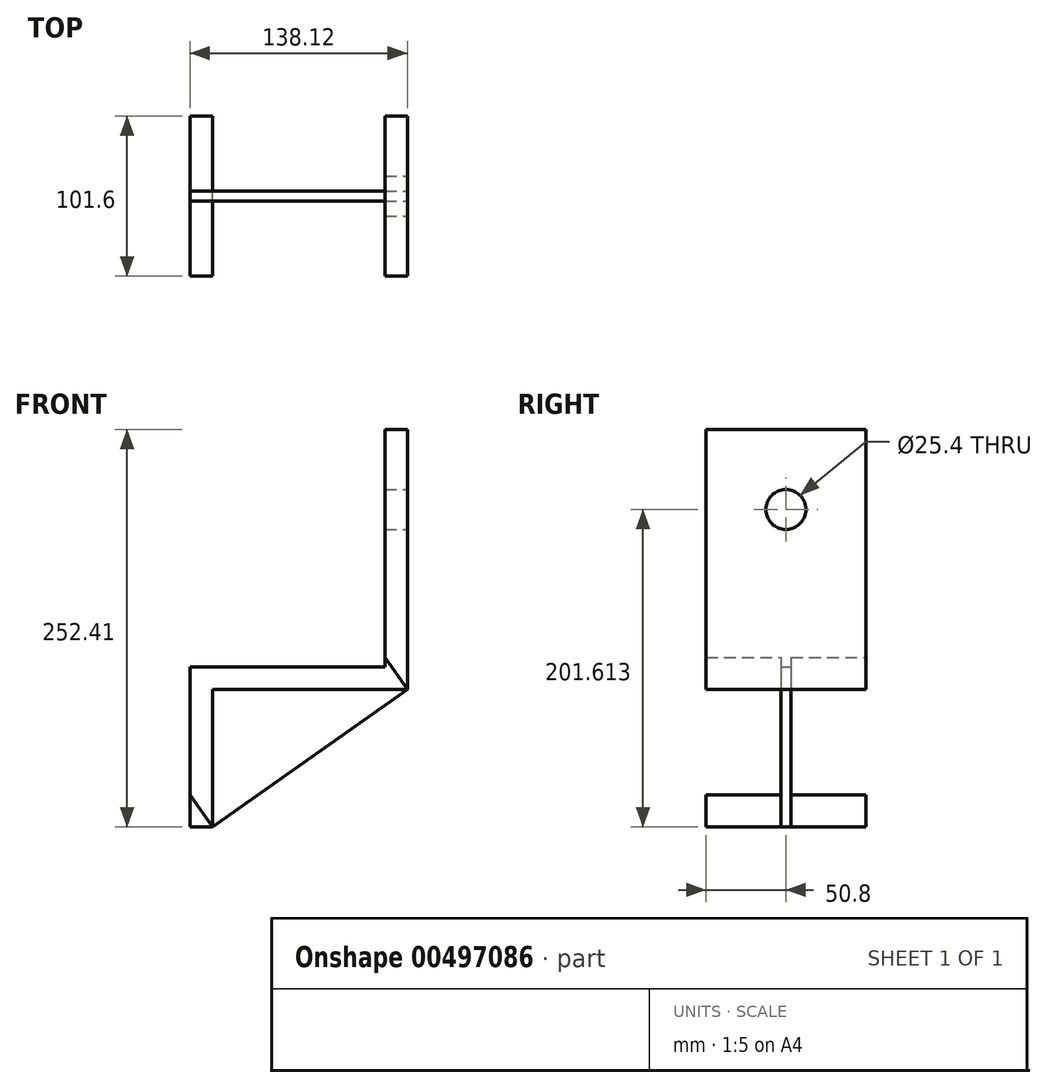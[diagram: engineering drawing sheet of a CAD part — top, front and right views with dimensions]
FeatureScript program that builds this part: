
annotation { "Feature Type Name" : "Feature", "Feature Type Description" : "" }
export const myFeature = defineFeature(function(context is Context, id is Id, definition is map)
    precondition{}
    {
        {
            var Q0;
            Q0=qCreatedBy(makeId("Front.planeOp"),FACE);
            var sketch = newSketch(context, id + "F0", { "sketchPlane" : qUnion([Q0])});
            skLineSegment(sketch, "E0", {"start": v(-37.87, -94.04) * mm, "end": v(-37.87, 7.56) * mm});
            skLineSegment(sketch, "E1", {"start": v(-37.87, 7.56) * mm, "end": v(85.96, 7.56) * mm});
            skLineSegment(sketch, "E2", {"start": v(85.96, 7.56) * mm, "end": v(85.96, 158.37) * mm});
            skLineSegment(sketch, "E3.0", {"start": v(100.25, -6.73) * mm, "end": v(100.25, 158.37) * mm});
            skLineSegment(sketch, "E3.1", {"start": v(-23.58, -6.73) * mm, "end": v(100.25, -6.73) * mm});
            skLineSegment(sketch, "E3.2", {"start": v(-23.58, -94.04) * mm, "end": v(-23.58, -6.73) * mm});
            skLineSegment(sketch, "E4", {"start": v(-37.87, -94.04) * mm, "end": v(-23.58, -94.04) * mm});
            skLineSegment(sketch, "E5", {"start": v(85.96, 158.37) * mm, "end": v(100.25, 158.37) * mm});
            skSolve(sketch);
        }
        {
            var Q0;
            Q0=makeQuery(id+"F0.imprint","IMPRINT",FACE,{"disambiguationData":[TD([[makeQuery(id+"F0.imprint","IMPRINT",EDGE,{"derivedFrom":sQuery(id+"F0.wireOp",EDGE,"E0")}),-1.0]])]});
            extrude(context, id + "F1", {"entities" : qUnion([Q0]), "depth" : 101.6 * mm});
        }
        {
            var Q0;
            Q0=makeQuery(id+"F1.opExtrude","SWEPT_FACE",FACE,{"disambiguationData":[OSD([sQuery(id+"F0.wireOp",EDGE,"E3.0")])]});
            var sketch = newSketch(context, id + "F2", { "sketchPlane" : qUnion([Q0])});
            skLineSegment(sketch, "E6", {"start": v(-50.8, 158.37) * mm, "end": v(-50.8, 107.57) * mm, "construction": true});
            skPoint(sketch, "E6.endSnap0", {"position": v(-50.8, 158.37) * mm});
            skSolve(sketch);
        }
        {
            var Q0;
            Q0=sQuery(id+"F2.wireOp",VERTEX,"E6.end");
            var Q1;
            Q1=makeQuery(id+"F1.opExtrude","SWEPT_BODY",BODY,{"disambiguationData":[OSD([sQuery(id+"F0.wireOp",EDGE,"E0"),sQuery(id+"F0.wireOp",EDGE,"E1"),sQuery(id+"F0.wireOp",EDGE,"E2"),sQuery(id+"F0.wireOp",EDGE,"E3.0"),sQuery(id+"F0.wireOp",EDGE,"E3.1"),sQuery(id+"F0.wireOp",EDGE,"E3.2"),sQuery(id+"F0.wireOp",EDGE,"E4"),sQuery(id+"F0.wireOp",EDGE,"E5")])]});
            hole(context, id + "F3", {"style" : HoleStyle.SIMPLE, "endStyle" : HoleEndStyle.THROUGH, "holeDiameter" : 25.4 * mm, "isTappedThrough" : true, "tappedDepth" : 12.7 * mm, "tapClearance" : 3, "startFromSketch" : true, "locations" : qUnion([Q0]), "scope" : qUnion([Q1])});
        }
        {
            var Q0;
            Q0=makeQuery(id+"F1.opExtrude","SWEPT_FACE",FACE,{"disambiguationData":[OSD([sQuery(id+"F0.wireOp",EDGE,"E3.2")])]});
            var sketch = newSketch(context, id + "F4", { "sketchPlane" : qUnion([Q0])});
            skLineSegment(sketch, "E7.bottom", {"start": v(-101.6, -94.04) * mm, "end": v(0, -94.04) * mm});
            skLineSegment(sketch, "E7.top", {"start": v(-101.6, -6.73) * mm, "end": v(0, -6.73) * mm});
            skLineSegment(sketch, "E7.left", {"start": v(-101.6, -94.04) * mm, "end": v(-101.6, -6.73) * mm});
            skLineSegment(sketch, "E7.right", {"start": v(0, -94.04) * mm, "end": v(0, -6.73) * mm});
            skSolve(sketch);
        }
        {
            var Q0;
            Q0 = qSketchRegion(id + "F4", true);
            var Q1;
            Q1=makeQuery(id+"F1.opExtrude","SWEPT_FACE",FACE,{"disambiguationData":[OSD([sQuery(id+"F0.wireOp",EDGE,"E3.0")])]});
            extrude(context, id + "F5", {"entities" : qUnion([Q0]), "endBound" : BoundingType.UP_TO_SURFACE, "endBoundEntityFace" : qUnion([Q1]), "depth" : 29.72 * mm});
        }
        {
            var Q0;
            Q0=makeQuery(id+"F5.opExtrude","SWEPT_FACE",FACE,{"disambiguationData":[OSD([sQuery(id+"F4.wireOp",EDGE,"E7.left")])]});
            var sketch = newSketch(context, id + "F6", { "sketchPlane" : qUnion([Q0])});
            skLineSegment(sketch, "E8", {"start": v(-23.58, -94.04) * mm, "end": v(100.25, -6.73) * mm});
            skSolve(sketch);
        }
        {
            var Q0;
            Q0=makeQuery(id+"F6.imprint","IMPRINT",FACE,{"disambiguationData":[TD([[makeQuery(id+"F6.imprint","IMPRINT",EDGE,{"derivedFrom":sQuery(id+"F6.wireOp",EDGE,"E8")}),-1.0]])]});
            extrude(context, id + "F7", {"entities" : qUnion([Q0]), "operationType" : NewBodyOperationType.REMOVE, "endBound" : BoundingType.THROUGH_ALL, "oppositeDirection" : true, "depth" : 25.4 * mm});
        }
        {
            var Q0;
            Q0=makeQuery(id+"F7.boolean.opBoolean","COPY",FACE,{"derivedFrom":makeQuery(id+"F7.opExtrude","SWEPT_FACE",FACE,{"disambiguationData":[OSD([sQuery(id+"F6.wireOp",EDGE,"E8")])]})});
            var sketch = newSketch(context, id + "F8", { "sketchPlane" : qUnion([Q0])});
            skLineSegment(sketch, "E9", {"start": v(-73.46, 50.8) * mm, "end": v(78.05, 50.8) * mm, "construction": true});
            skLineSegment(sketch, "E10.0", {"start": v(-73.46, 47.63) * mm, "end": v(78.05, 47.63) * mm});
            skLineSegment(sketch, "E11.MirrorCS", {"start": v(-73.46, 53.98) * mm, "end": v(78.05, 53.98) * mm});
            skSolve(sketch);
        }
        {
            var Q0;
            {var subQ0=sQuery(id+"F8.wireOp",EDGE,"E11.MirrorCS");Q0=makeQuery(id+"F8.imprint","IMPRINT",FACE,{"disambiguationData":[TD([[makeQuery(id+"F8.imprint","IMPRINT",EDGE,{"derivedFrom":subQ0}),1.0]])]});}
            extrude(context, id + "F9", {"entities" : qUnion([Q0]), "operationType" : NewBodyOperationType.REMOVE, "endBound" : BoundingType.THROUGH_ALL, "oppositeDirection" : true, "depth" : 25.4 * mm});
        }
        {
            var Q0;
            {var subQ0=sQuery(id+"F8.wireOp",EDGE,"E10.0");Q0=makeQuery(id+"F8.imprint","IMPRINT",FACE,{"disambiguationData":[TD([[makeQuery(id+"F8.imprint","IMPRINT",EDGE,{"derivedFrom":subQ0}),-1.0]])]});}
            extrude(context, id + "F10", {"entities" : qUnion([Q0]), "operationType" : NewBodyOperationType.REMOVE, "endBound" : BoundingType.THROUGH_ALL, "oppositeDirection" : true, "depth" : 25.4 * mm});
        }
    });
